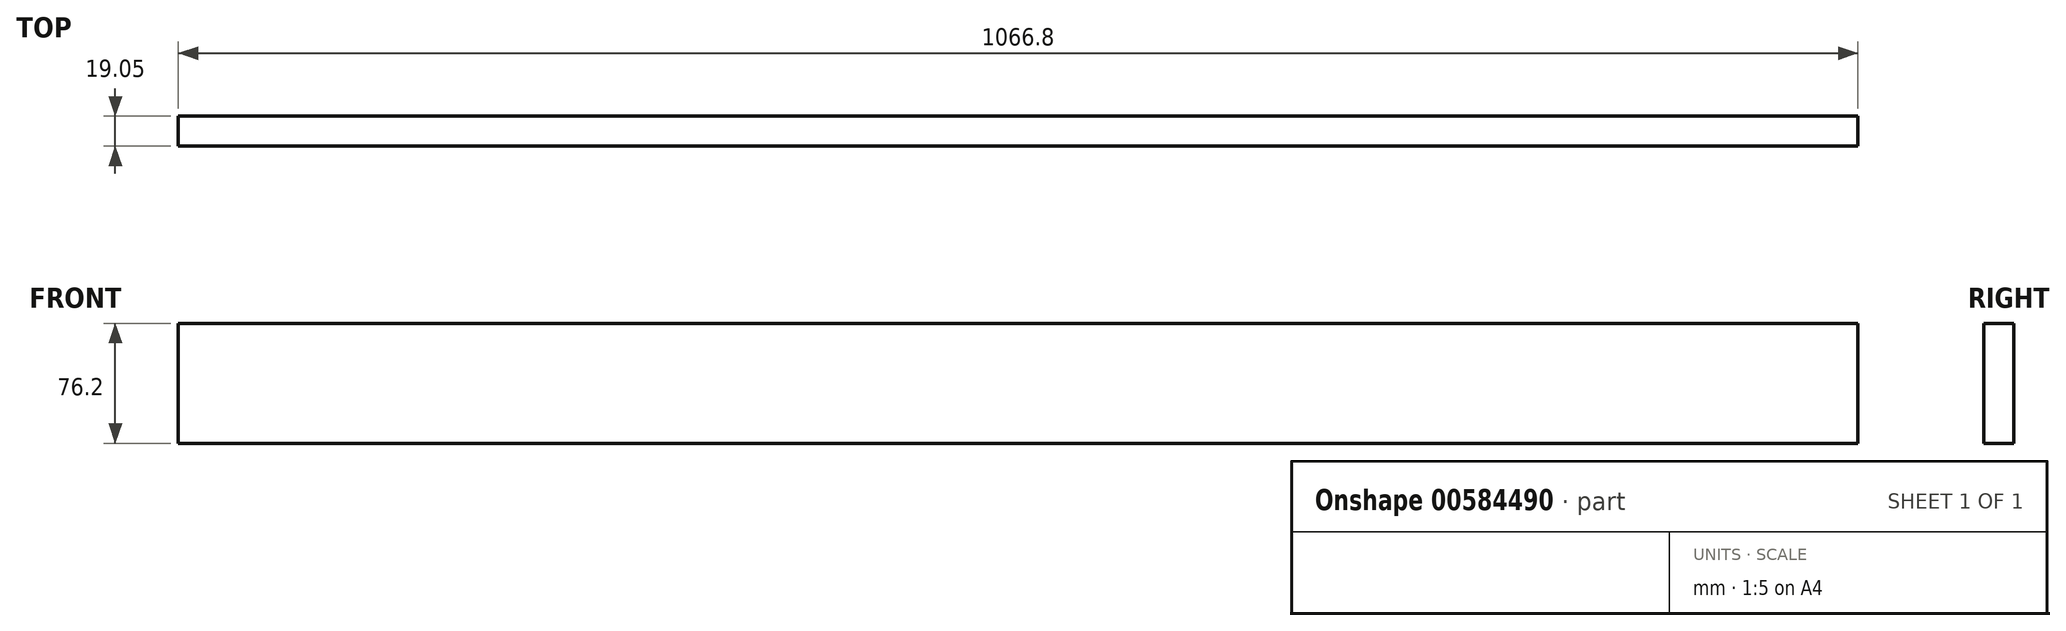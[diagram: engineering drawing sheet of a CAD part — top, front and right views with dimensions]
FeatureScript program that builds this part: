
annotation { "Feature Type Name" : "Feature", "Feature Type Description" : "" }
export const myFeature = defineFeature(function(context is Context, id is Id, definition is map)
    precondition{}
    {
        {
            var Q0;
            Q0=qCreatedBy(makeId("Front.planeOp"),FACE);
            var sketch = newSketch(context, id + "F0", { "sketchPlane" : qUnion([Q0])});
            skLineSegment(sketch, "E0.bottom", {"start": v(0, 0) * mm, "end": v(1066.8, 0) * mm});
            skLineSegment(sketch, "E0.top", {"start": v(0, 76.2) * mm, "end": v(1066.8, 76.2) * mm});
            skLineSegment(sketch, "E0.left", {"start": v(0, 0) * mm, "end": v(0, 76.2) * mm});
            skLineSegment(sketch, "E0.right", {"start": v(1066.8, 0) * mm, "end": v(1066.8, 76.2) * mm});
            skSolve(sketch);
        }
        {
            var Q0;
            Q0=makeQuery(id+"F0.imprint","IMPRINT",FACE,{"disambiguationData":[TD([[makeQuery(id+"F0.imprint","IMPRINT",EDGE,{"derivedFrom":sQuery(id+"F0.wireOp",EDGE,"E0.bottom")}),1.0]])]});
            extrude(context, id + "F1", {"entities" : qUnion([Q0]), "depth" : 19.05 * mm, "offsetDistance" : 25.4 * mm});
        }
    });
